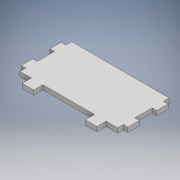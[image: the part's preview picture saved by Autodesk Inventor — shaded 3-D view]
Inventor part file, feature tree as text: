
AUTODESK INVENTOR PART (.ipt)
format: ipt  version: 2018 (Build 220112000, 112)  size: 146,944 bytes
history: native  units: mm
features: extrude x3, sketch x3, plane x1, mirror x1, projected_geometry x1
ambient origin geometry x8: Origin, YZ Plane, XZ Plane, XY Plane, X Axis, Y Axis, Z Axis, Center Point
bodies: Solid1 (feature_tree)
feature tree (9):
  extrude  "Extrusion1"  Depth=45.0mm
  extrude  "Extrusion2"  Depth=4.0mm
  plane  "Work Plane1"
  mirror  "Mirror1"
  extrude  "Extrusion3"  Depth=10.0mm
  sketch  "Sketch1"  dims[d0=85.0mm d1=45.0mm]
  sketch  "Sketch2"  dims[d2=4.0mm d3=0.0mm d4=4.0mm]
  projected_geometry  "Projected Loop1"
  sketch  "Sketch3"  dims[d5=10.0mm d6=10.0mm d7=5.0mm d8=5.0mm d9=4.0mm d10=0.0mm d11=10.0mm d12=8.0mm d13=10.0mm d14=8.0mm d16=4.0mm d17=0.0mm d19=10.0mm]
